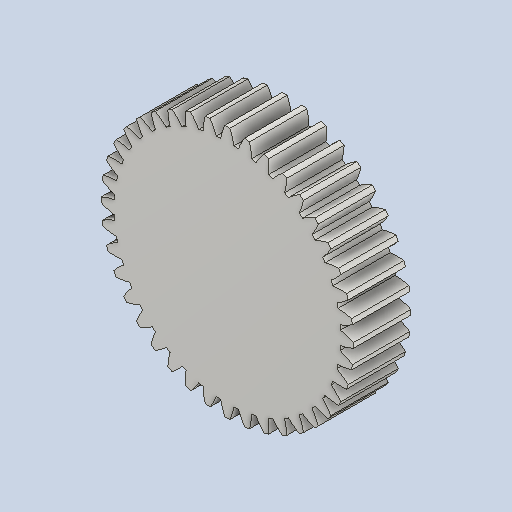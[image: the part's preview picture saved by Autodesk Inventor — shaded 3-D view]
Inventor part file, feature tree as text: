
AUTODESK INVENTOR PART (.ipt)
format: ipt  version: 2023 (Build 270158000, 158)  size: 308,224 bytes
history: native  units: mm (DEFAULTED — no unit token found)
features: plane x3, other x3, sketch x2, extrude x1
ambient origin geometry x8: Origin, YZ Plane, XZ Plane, XY Plane, X Axis, Y Axis, Z Axis, Center Point
bodies: Solid1 (feature_tree)
feature tree (9):
  extrude  "Extrusion1"  Depth=20.0mm TaperAngle=0.0deg
  plane  "Work Plane2"
  plane  "Work Plane8"
  plane  "Work Plane9"
  other  "Spur Gear"
  sketch  "Sketch1"  dims[d0=88.0mm d1=20.0mm d2=0.0mm]
  sketch  "Sketch2"  dims[d3=80.0mm d4=10.0mm d5=0.0mm d16=200.0mm d17=0.0mm d34=0.785398mm d39=0.0mm d41=0.0mm d43=200.0mm d46=200.0mm d47=0.0mm d48=0.0mm]
  other  "Srf1"
  other  "Pitch Diameter"
